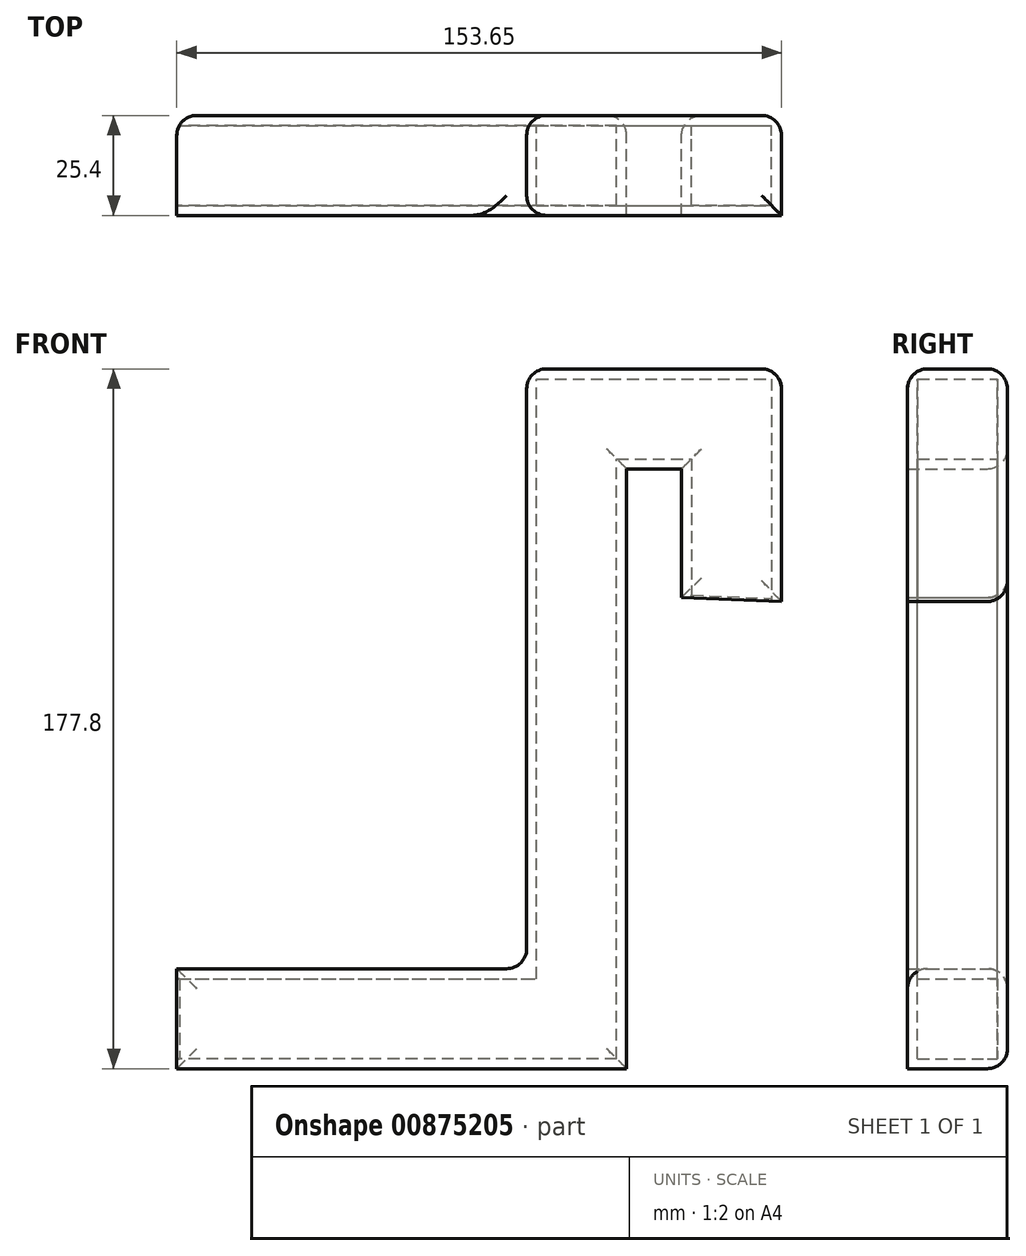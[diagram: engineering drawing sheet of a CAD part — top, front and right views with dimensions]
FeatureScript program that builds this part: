
annotation { "Feature Type Name" : "Feature", "Feature Type Description" : "" }
export const myFeature = defineFeature(function(context is Context, id is Id, definition is map)
    precondition{}
    {
        {
            var Q0;
            Q0=qCreatedBy(makeId("Front.planeOp"),FACE);
            var sketch = newSketch(context, id + "F0", { "sketchPlane" : qUnion([Q0])});
            skLineSegment(sketch, "E0", {"start": v(-47.97, -57.36) * mm, "end": v(-47.97, 95.04) * mm});
            skLineSegment(sketch, "E1", {"start": v(-47.97, 95.04) * mm, "end": v(-34.02, 95.04) * mm});
            skLineSegment(sketch, "E2", {"start": v(-34.02, 95.04) * mm, "end": v(-34.02, 62.4) * mm});
            skLineSegment(sketch, "E3", {"start": v(-73.37, 93.72) * mm, "end": v(-73.37, 120.44) * mm});
            skLineSegment(sketch, "E4", {"start": v(-73.37, 120.44) * mm, "end": v(-8.62, 120.44) * mm});
            skLineSegment(sketch, "E5", {"start": v(-8.62, 120.44) * mm, "end": v(-8.62, 61.34) * mm});
            skLineSegment(sketch, "E6", {"start": v(-8.62, 61.34) * mm, "end": v(-34.02, 62.4) * mm});
            skLineSegment(sketch, "E7", {"start": v(-47.97, -57.36) * mm, "end": v(-162.27, -57.36) * mm});
            skLineSegment(sketch, "E8", {"start": v(-162.27, -57.36) * mm, "end": v(-162.27, -31.96) * mm});
            skLineSegment(sketch, "E9", {"start": v(-162.27, -31.96) * mm, "end": v(-73.37, -31.96) * mm});
            skLineSegment(sketch, "E10", {"start": v(-73.37, -31.96) * mm, "end": v(-73.37, 93.72) * mm});
            skSolve(sketch);
        }
        {
            var Q0;
            Q0=makeQuery(id+"F0.imprint","IMPRINT",FACE,{"disambiguationData":[TD([[makeQuery(id+"F0.imprint","IMPRINT",EDGE,{"derivedFrom":sQuery(id+"F0.wireOp",EDGE,"E0")}),1.0]])]});
            extrude(context, id + "F1", {"entities" : qUnion([Q0]), "depth" : 25.4 * mm, "offsetDistance" : 25.4 * mm});
        }
        {
            var Q0;
            Q0=makeQuery(id+"F1.opExtrude","SWEPT_FACE",FACE,{"disambiguationData":[OSD([sQuery(id+"F0.wireOp",EDGE,"E8")])]});
            var Q1;
            Q1=makeQuery(id+"F1.opExtrude","SWEPT_FACE",FACE,{"disambiguationData":[OSD([sQuery(id+"F0.wireOp",EDGE,"E6")])]});
            shell(context, id + "F2", {"entities" : qUnion([Q0, Q1]), "thickness" : 2.54 * mm});
        }
        {
            var Q0;
            Q0=makeQuery(id+"F1.opExtrude","SWEPT_FACE",FACE,{"disambiguationData":[OSD([sQuery(id+"F0.wireOp",EDGE,"E3"),sQuery(id+"F0.wireOp",EDGE,"E10")])]});
            var Q1;
            Q1=makeQuery(id+"F1.opExtrude","CAP_EDGE",EDGE,{"disambiguationData":[OSD([sQuery(id+"F0.wireOp",EDGE,"E3"),sQuery(id+"F0.wireOp",EDGE,"E10")])],"isStart":false});
            var Q2;
            Q2=makeQuery(id+"F1.opExtrude","SWEPT_FACE",FACE,{"disambiguationData":[OSD([sQuery(id+"F0.wireOp",EDGE,"E4")])]});
            var Q3;
            Q3=makeQuery(id+"F1.opExtrude","CAP_FACE",FACE,{"disambiguationData":[OSD([sQuery(id+"F0.wireOp",EDGE,"E0"),sQuery(id+"F0.wireOp",EDGE,"E1"),sQuery(id+"F0.wireOp",EDGE,"E2"),sQuery(id+"F0.wireOp",EDGE,"E3"),sQuery(id+"F0.wireOp",EDGE,"E4"),sQuery(id+"F0.wireOp",EDGE,"E5"),sQuery(id+"F0.wireOp",EDGE,"E6"),sQuery(id+"F0.wireOp",EDGE,"E7"),sQuery(id+"F0.wireOp",EDGE,"E8"),sQuery(id+"F0.wireOp",EDGE,"E9"),sQuery(id+"F0.wireOp",EDGE,"E10")])],"isStart":true});
            fillet(context, id + "F3", {"entities" : qUnion([Q0, Q1, Q2, Q3]), "radius" : 5.08 * mm, "tangentPropagation" : true, "allowEdgeOverflow" : false});
        }
    });
